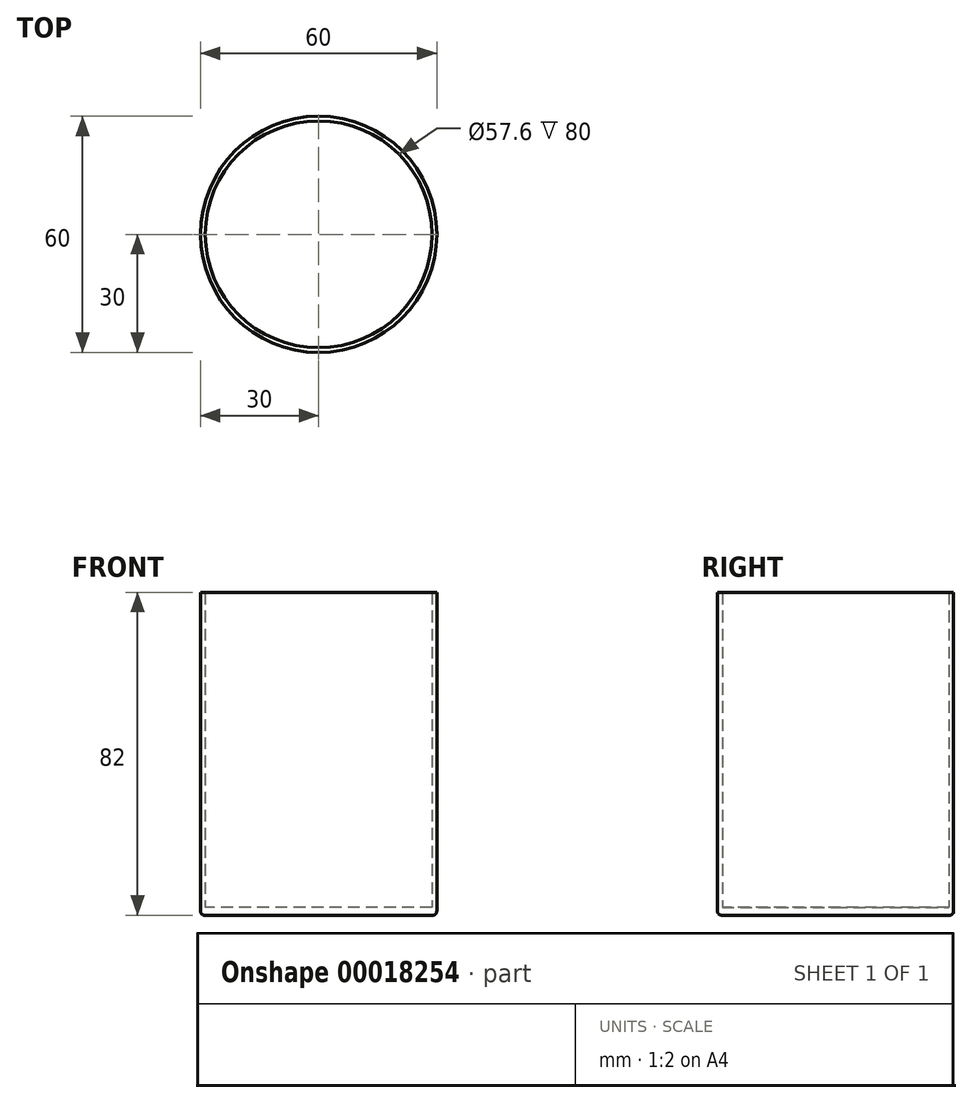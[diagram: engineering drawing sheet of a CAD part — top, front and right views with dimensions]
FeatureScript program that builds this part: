
annotation { "Feature Type Name" : "Feature", "Feature Type Description" : "" }
export const myFeature = defineFeature(function(context is Context, id is Id, definition is map)
    precondition{}
    {
        {
            var Q0;
            Q0=qCreatedBy(makeId("Top.planeOp"),FACE);
            var sketch = newSketch(context, id + "F0", { "sketchPlane" : qUnion([Q0])});
            skCircle(sketch, "E0", {"center": v(0, 0) * mm, "radius": 30 * mm});
            skSolve(sketch);
        }
        {
            var Q0;
            Q0=makeQuery(id+"F0.imprint","IMPRINT",FACE,{"disambiguationData":[TD([[makeQuery(id+"F0.imprint","IMPRINT",EDGE,{"derivedFrom":sQuery(id+"F0.wireOp",EDGE,"E0")}),1.0]])]});
            extrude(context, id + "F1", {"entities" : qUnion([Q0]), "depth" : 2 * mm});
        }
        {
            var Q0;
            Q0=makeQuery(id+"F1.opExtrude","CAP_FACE",FACE,{"disambiguationData":[OSD([sQuery(id+"F0.wireOp",EDGE,"E0")])],"isStart":false});
            var sketch = newSketch(context, id + "F2", { "sketchPlane" : qUnion([Q0])});
            skCircle(sketch, "E1", {"center": v(0, 0) * mm, "radius": 30 * mm});
            skCircle(sketch, "E2", {"center": v(0, 0) * mm, "radius": 28.8 * mm});
            skSolve(sketch);
        }
        {
            var Q0;
            Q0=makeQuery(id+"F2.imprint","IMPRINT",FACE,{"disambiguationData":[TD([[makeQuery(id+"F2.imprint","IMPRINT",EDGE,{"derivedFrom":sQuery(id+"F2.wireOp",EDGE,"E1")}),1.0]])]});
            extrude(context, id + "F3", {"entities" : qUnion([Q0]), "operationType" : NewBodyOperationType.ADD, "depth" : 80 * mm});
        }
        {
            var Q0;
            Q0=makeQuery(id+"F3.opExtrude","CAP_EDGE",EDGE,{"disambiguationData":[OSD([sQuery(id+"F2.wireOp",EDGE,"E2")])],"isStart":true});
            var Q1;
            Q1=makeQuery(id+"F1.opExtrude","CAP_EDGE",EDGE,{"disambiguationData":[OSD([sQuery(id+"F0.wireOp",EDGE,"E0")])],"isStart":true});
            fillet(context, id + "F4", {"entities" : qUnion([Q0, Q1]), "radius" : 1 * mm, "tangentPropagation" : true, "allowEdgeOverflow" : false});
        }
    });
